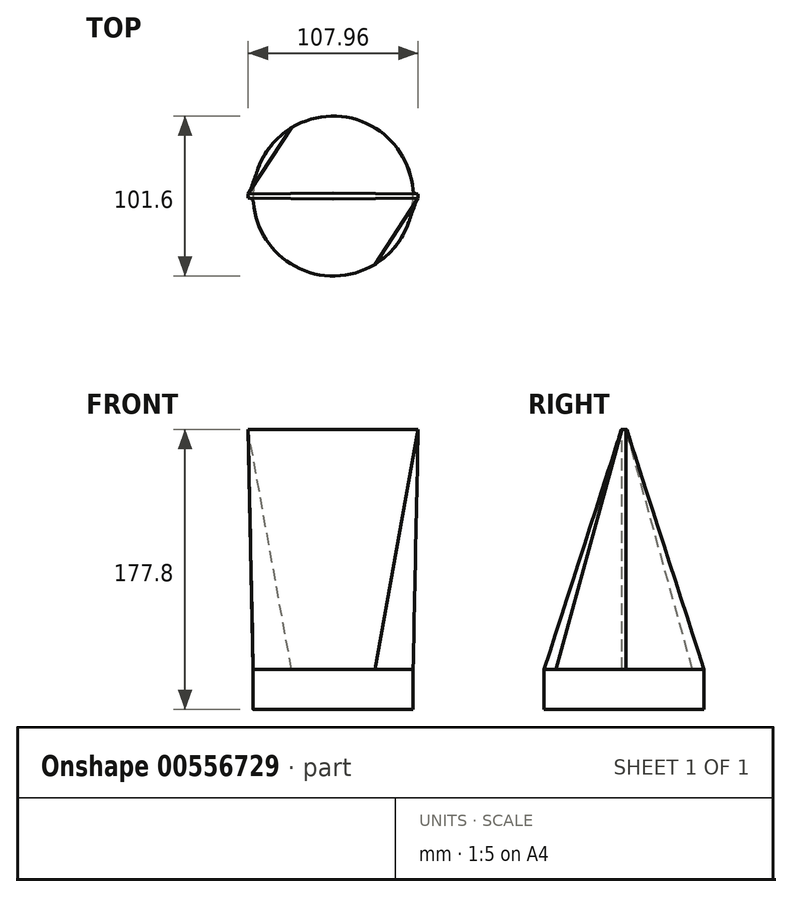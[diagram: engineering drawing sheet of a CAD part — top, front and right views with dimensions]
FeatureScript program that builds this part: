
annotation { "Feature Type Name" : "Feature", "Feature Type Description" : "" }
export const myFeature = defineFeature(function(context is Context, id is Id, definition is map)
    precondition{}
    {
        {
            var Q0;
            Q0=qCreatedBy(makeId("Top.planeOp"),FACE);
            cPlane(context, id + "F0", {"entities" : qUnion([Q0]), "cplaneType" : CPlaneType.OFFSET, "offset" : 152.4 * mm, "width" : 152.4 * mm, "height" : 152.4 * mm});
        }
        {
            var Q0;
            Q0=qCreatedBy(makeId("Top.planeOp"),FACE);
            var sketch = newSketch(context, id + "F1", { "sketchPlane" : qUnion([Q0])});
            skCircle(sketch, "E0", {"center": v(0, 0) * mm, "radius": 50.8 * mm});
            skSolve(sketch);
        }
        {
            var Q0;
            Q0=qCreatedBy(id+"F0.planeOp",FACE);
            var sketch = newSketch(context, id + "F2", { "sketchPlane" : qUnion([Q0])});
            skLineSegment(sketch, "E1.left", {"start": v(53.98, 1.27) * mm, "end": v(53.98, -1.27) * mm});
            skLineSegment(sketch, "E1.right", {"start": v(-53.98, 1.27) * mm, "end": v(-53.98, -1.27) * mm});
            skPoint(sketch, "E1.middle", {"position": v(0, 0) * mm});
            skLineSegment(sketch, "E2", {"start": v(-53.98, 1.27) * mm, "end": v(0, 1.9) * mm});
            skLineSegment(sketch, "E3", {"start": v(0, 1.9) * mm, "end": v(53.98, 1.27) * mm});
            skLineSegment(sketch, "E4", {"start": v(53.98, -1.27) * mm, "end": v(0, -1.9) * mm});
            skLineSegment(sketch, "E5", {"start": v(0, -1.9) * mm, "end": v(-53.97, -1.27) * mm});
            skSolve(sketch);
        }
        {
            var Q0;
            Q0=makeQuery(id+"F1.imprint","IMPRINT",FACE,{"disambiguationData":[TD([[makeQuery(id+"F1.imprint","IMPRINT",EDGE,{"derivedFrom":sQuery(id+"F1.wireOp",EDGE,"E0")}),1.0]])]});
            var Q1;
            Q1=makeQuery(id+"F2.imprint","IMPRINT",FACE,{"disambiguationData":[TD([[makeQuery(id+"F2.imprint","IMPRINT",EDGE,{"derivedFrom":sQuery(id+"F2.wireOp",EDGE,"E1.left")}),-1.0]])]});
            loft(context, id + "F3", {"sheetProfilesArray" : [{ "sheetProfileEntities" : qUnion([Q0]) }, { "sheetProfileEntities" : qUnion([Q1]) }]});
        }
        {
            var Q0;
            Q0=makeQuery(id+"F3.opLoft","CAP_FACE",FACE,{"disambiguationData":[OSD([makeQuery(id+"F1.imprint","IMPRINT",FACE,{"disambiguationData":[TD([[makeQuery(id+"F1.imprint","IMPRINT",EDGE,{"derivedFrom":sQuery(id+"F1.wireOp",EDGE,"E0")}),1.0]])]})])],"isStart":true});
            var sketch = newSketch(context, id + "F4", { "sketchPlane" : qUnion([Q0])});
            skCircle(sketch, "E6", {"center": v(0, 0) * mm, "radius": 50.8 * mm});
            skSolve(sketch);
        }
        {
            var Q0;
            Q0 = qSketchRegion(id + "F4", true);
            extrude(context, id + "F5", {"entities" : qUnion([Q0]), "depth" : 25.4 * mm, "offsetDistance" : 25.4 * mm});
        }
    });
